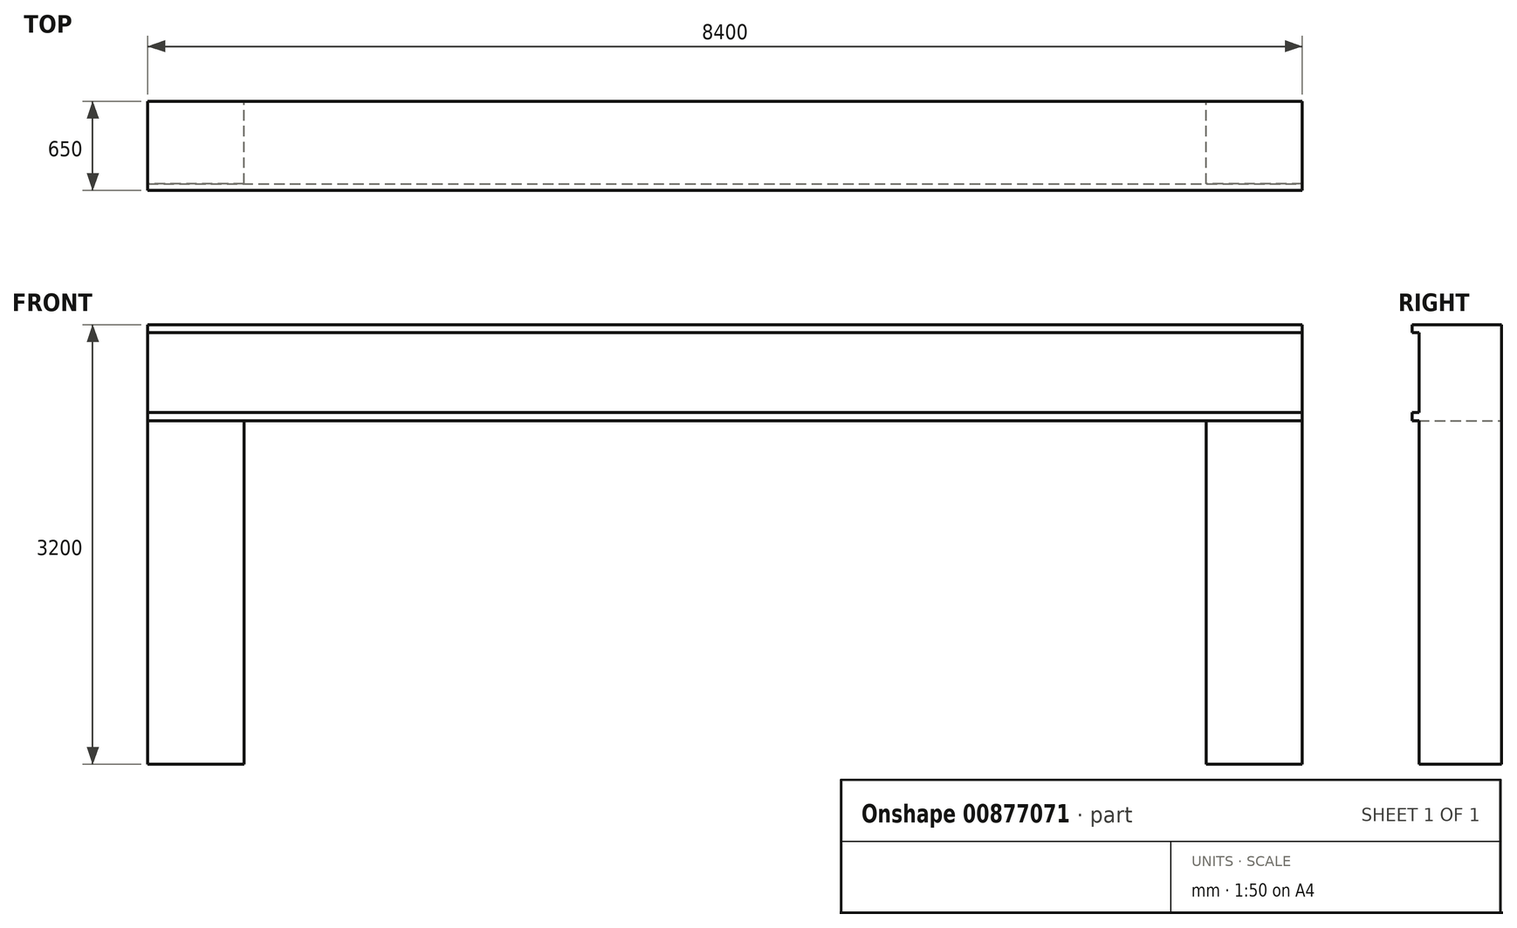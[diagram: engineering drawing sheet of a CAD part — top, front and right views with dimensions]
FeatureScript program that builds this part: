
annotation { "Feature Type Name" : "Feature", "Feature Type Description" : "" }
export const myFeature = defineFeature(function(context is Context, id is Id, definition is map)
    precondition{}
    {
        {
            var Q0;
            Q0=qCreatedBy(makeId("Front.planeOp"),FACE);
            var sketch = newSketch(context, id + "F0", { "sketchPlane" : qUnion([Q0])});
            skLineSegment(sketch, "E0.bottom", {"start": v(4200, 1600) * mm, "end": v(-4200, 1600) * mm});
            skLineSegment(sketch, "E0.top", {"start": v(4200, -1600) * mm, "end": v(3500, -1600) * mm});
            skLineSegment(sketch, "E0.left", {"start": v(4200, 1600) * mm, "end": v(4200, -1600) * mm});
            skLineSegment(sketch, "E0.right", {"start": v(-4200, 1600) * mm, "end": v(-4200, -1600) * mm});
            skPoint(sketch, "E0.middle", {"position": v(0, 0) * mm});
            skLineSegment(sketch, "E1.0", {"start": v(-3500, 900) * mm, "end": v(-3500, -1600) * mm});
            skLineSegment(sketch, "E1.1", {"start": v(3500, 900) * mm, "end": v(-3500, 900) * mm});
            skLineSegment(sketch, "E1.2", {"start": v(3500, 900) * mm, "end": v(3500, -1600) * mm});
            skLineSegment(sketch, "E2.trimOffspring", {"start": v(-3500, -1600) * mm, "end": v(-4200, -1600) * mm});
            skSolve(sketch);
        }
        {
            var Q0;
            Q0=makeQuery(id+"F0.imprint","IMPRINT",FACE,{"disambiguationData":[TD([[makeQuery(id+"F0.imprint","IMPRINT",EDGE,{"derivedFrom":sQuery(id+"F0.wireOp",EDGE,"E0.bottom")}),1.0]])]});
            extrude(context, id + "F1", {"entities" : qUnion([Q0]), "depth" : 600 * mm, "offsetDistance" : 25 * mm});
        }
        {
            var Q0;
            Q0=makeQuery(id+"F1.opExtrude","CAP_FACE",FACE,{"disambiguationData":[OSD([sQuery(id+"F0.wireOp",EDGE,"E0.bottom"),sQuery(id+"F0.wireOp",EDGE,"E0.top"),sQuery(id+"F0.wireOp",EDGE,"E0.left"),sQuery(id+"F0.wireOp",EDGE,"E0.right"),sQuery(id+"F0.wireOp",EDGE,"E1.0"),sQuery(id+"F0.wireOp",EDGE,"E1.1"),sQuery(id+"F0.wireOp",EDGE,"E1.2"),sQuery(id+"F0.wireOp",EDGE,"E2.trimOffspring")])],"isStart":false});
            var sketch = newSketch(context, id + "F2", { "sketchPlane" : qUnion([Q0])});
            skLineSegment(sketch, "E3.bottom", {"start": v(-4200, 1600) * mm, "end": v(4200, 1600) * mm});
            skLineSegment(sketch, "E3.top", {"start": v(-4200, 1540) * mm, "end": v(4200, 1540) * mm});
            skLineSegment(sketch, "E3.left", {"start": v(-4200, 1600) * mm, "end": v(-4200, 1540) * mm});
            skLineSegment(sketch, "E3.right", {"start": v(4200, 1600) * mm, "end": v(4200, 1540) * mm});
            skLineSegment(sketch, "E4.bottom", {"start": v(-4200, 900) * mm, "end": v(4200, 900) * mm});
            skLineSegment(sketch, "E4.top", {"start": v(-4200, 960) * mm, "end": v(4200, 960) * mm});
            skLineSegment(sketch, "E4.left", {"start": v(-4200, 900) * mm, "end": v(-4200, 960) * mm});
            skLineSegment(sketch, "E4.right", {"start": v(4200, 900) * mm, "end": v(4200, 960) * mm});
            skSolve(sketch);
        }
        {
            var Q0;
            Q0=makeQuery(id+"F2.imprint","IMPRINT",FACE,{"disambiguationData":[TD([[makeQuery(id+"F2.imprint","IMPRINT",EDGE,{"derivedFrom":sQuery(id+"F2.wireOp",EDGE,"E3.bottom")}),1.0]])]});
            var Q1;
            Q1=makeQuery(id+"F2.imprint","IMPRINT",FACE,{"disambiguationData":[TD([[makeQuery(id+"F2.imprint","IMPRINT",EDGE,{"derivedFrom":sQuery(id+"F2.wireOp",EDGE,"E4.top")}),-1.0]])]});
            extrude(context, id + "F3", {"entities" : qUnion([Q0, Q1]), "operationType" : NewBodyOperationType.ADD, "depth" : 50 * mm, "offsetDistance" : 25 * mm});
        }
    });
